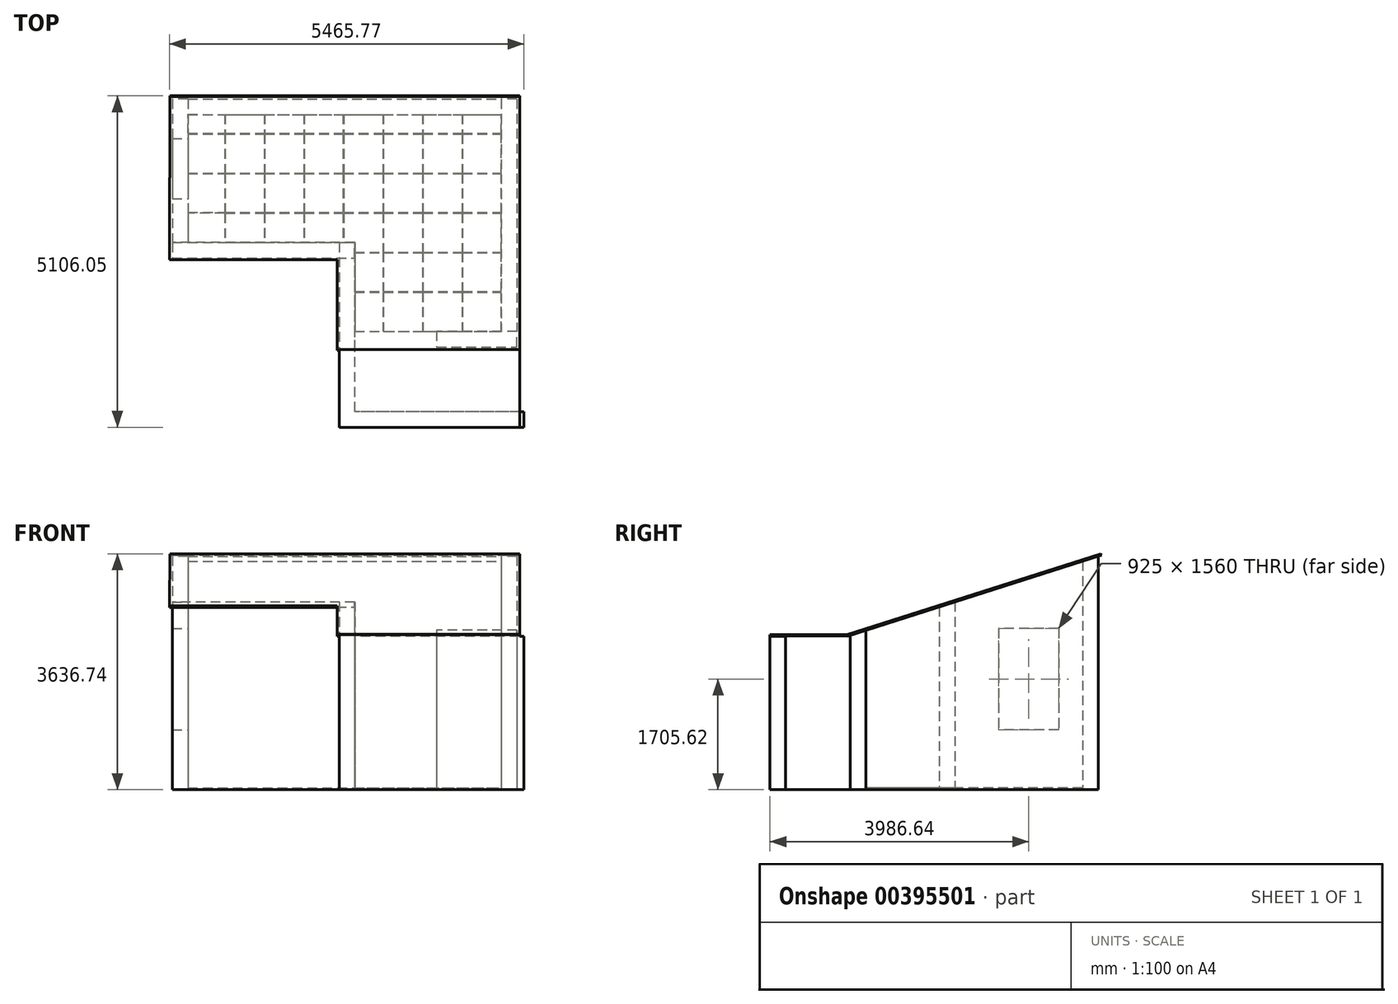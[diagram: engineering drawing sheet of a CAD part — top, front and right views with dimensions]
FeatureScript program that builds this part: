
annotation { "Feature Type Name" : "Feature", "Feature Type Description" : "" }
export const myFeature = defineFeature(function(context is Context, id is Id, definition is map)
    precondition{}
    {
        {
            var Q0;
            Q0=qCreatedBy(makeId("Top.planeOp"),FACE);
            var sketch = newSketch(context, id + "F0", { "sketchPlane" : qUnion([Q0])});
            skLineSegment(sketch, "E0.bottom", {"start": v(-2414.8, 666.08) * mm, "end": v(2415.2, 666.08) * mm});
            skLineSegment(sketch, "E0.top", {"start": v(155.2, -2673.92) * mm, "end": v(2415.2, -2673.92) * mm});
            skLineSegment(sketch, "E0.left", {"start": v(-2414.8, 666.08) * mm, "end": v(-2414.8, -1303.92) * mm});
            skLineSegment(sketch, "E0.right", {"start": v(2415.2, 666.08) * mm, "end": v(2415.2, -2673.92) * mm});
            skLineSegment(sketch, "E1.bottom", {"start": v(-2414.8, -1303.92) * mm, "end": v(155.2, -1303.92) * mm});
            skLineSegment(sketch, "E2", {"start": v(155.2, -1303.92) * mm, "end": v(155.2, -2673.92) * mm});
            skLineSegment(sketch, "E3.top", {"start": v(1817.14, -2673.92) * mm, "end": v(2415.2, -2673.92) * mm});
            skLineSegment(sketch, "E4.top", {"start": v(1208.14, -2673.92) * mm, "end": v(1808.14, -2673.92) * mm});
            skLineSegment(sketch, "E5.top", {"start": v(597, -2673.92) * mm, "end": v(1197, -2673.92) * mm});
            skLineSegment(sketch, "E6.top", {"start": v(155.2, -2673.92) * mm, "end": v(588, -2673.92) * mm});
            skSolve(sketch);
        }
        {
            var Q0;
            Q0=qCreatedBy(makeId("Top.planeOp"),FACE);
            var sketch = newSketch(context, id + "F1", { "sketchPlane" : qUnion([Q0])});
            skLineSegment(sketch, "E7.bottom", {"start": v(1816.8, -2073.43) * mm, "end": v(2414.86, -2073.43) * mm});
            skLineSegment(sketch, "E7.top", {"start": v(1816.8, -2673.43) * mm, "end": v(2414.86, -2673.43) * mm});
            skLineSegment(sketch, "E7.left", {"start": v(1816.8, -2073.43) * mm, "end": v(1816.8, -2673.43) * mm});
            skLineSegment(sketch, "E8.bottom", {"start": v(1816.8, -1461.43) * mm, "end": v(2414.86, -1461.43) * mm});
            skLineSegment(sketch, "E8.top", {"start": v(1816.8, -2061.43) * mm, "end": v(2414.86, -2061.43) * mm});
            skLineSegment(sketch, "E8.left", {"start": v(1816.8, -1461.43) * mm, "end": v(1816.8, -2061.43) * mm});
            skLineSegment(sketch, "E9.bottom", {"start": v(1816.8, -854.43) * mm, "end": v(2414.86, -854.43) * mm});
            skLineSegment(sketch, "E9.top", {"start": v(1816.8, -1454.43) * mm, "end": v(2414.86, -1454.43) * mm});
            skLineSegment(sketch, "E9.left", {"start": v(1816.8, -854.43) * mm, "end": v(1816.8, -1454.43) * mm});
            skLineSegment(sketch, "E10.bottom", {"start": v(1816.8, -242.43) * mm, "end": v(2414.86, -242.43) * mm});
            skLineSegment(sketch, "E10.top", {"start": v(1816.8, -842.43) * mm, "end": v(2414.86, -842.43) * mm});
            skLineSegment(sketch, "E10.left", {"start": v(1816.8, -242.43) * mm, "end": v(1816.8, -842.43) * mm});
            skLineSegment(sketch, "E11.bottom", {"start": v(1816.8, 365.57) * mm, "end": v(2414.86, 365.57) * mm});
            skLineSegment(sketch, "E11.top", {"start": v(1816.8, -234.43) * mm, "end": v(2414.86, -234.43) * mm});
            skLineSegment(sketch, "E11.left", {"start": v(1816.8, 365.57) * mm, "end": v(1816.8, -234.43) * mm});
            skLineSegment(sketch, "E12.top", {"start": v(1816.8, 377.57) * mm, "end": v(2414.86, 377.57) * mm});
            skLineSegment(sketch, "E12.left", {"start": v(1816.8, 666.57) * mm, "end": v(1816.8, 377.57) * mm});
            skLineSegment(sketch, "E13.bottom", {"start": v(1207.8, -2073.43) * mm, "end": v(1807.8, -2073.43) * mm});
            skLineSegment(sketch, "E13.top", {"start": v(1207.8, -2673.43) * mm, "end": v(1807.8, -2673.43) * mm});
            skLineSegment(sketch, "E13.left", {"start": v(1207.8, -2073.43) * mm, "end": v(1207.8, -2673.43) * mm});
            skLineSegment(sketch, "E13.right", {"start": v(1807.8, -2073.43) * mm, "end": v(1807.8, -2673.43) * mm});
            skLineSegment(sketch, "E14.bottom", {"start": v(1207.8, -1461.43) * mm, "end": v(1807.8, -1461.43) * mm});
            skLineSegment(sketch, "E14.top", {"start": v(1207.8, -2061.43) * mm, "end": v(1807.8, -2061.43) * mm});
            skLineSegment(sketch, "E14.left", {"start": v(1207.8, -1461.43) * mm, "end": v(1207.8, -2061.43) * mm});
            skLineSegment(sketch, "E14.right", {"start": v(1807.8, -1461.43) * mm, "end": v(1807.8, -2061.43) * mm});
            skLineSegment(sketch, "E15.bottom", {"start": v(1207.8, -854.43) * mm, "end": v(1807.8, -854.43) * mm});
            skLineSegment(sketch, "E15.top", {"start": v(1207.8, -1454.43) * mm, "end": v(1807.8, -1454.43) * mm});
            skLineSegment(sketch, "E15.left", {"start": v(1207.8, -854.43) * mm, "end": v(1207.8, -1454.43) * mm});
            skLineSegment(sketch, "E15.right", {"start": v(1807.8, -854.43) * mm, "end": v(1807.8, -1454.43) * mm});
            skLineSegment(sketch, "E16.bottom", {"start": v(1207.8, -242.43) * mm, "end": v(1807.8, -242.43) * mm});
            skLineSegment(sketch, "E16.top", {"start": v(1207.8, -842.43) * mm, "end": v(1807.8, -842.43) * mm});
            skLineSegment(sketch, "E16.left", {"start": v(1207.8, -242.43) * mm, "end": v(1207.8, -842.43) * mm});
            skLineSegment(sketch, "E16.right", {"start": v(1807.8, -242.43) * mm, "end": v(1807.8, -842.43) * mm});
            skLineSegment(sketch, "E17.bottom", {"start": v(1207.8, 365.57) * mm, "end": v(1807.8, 365.57) * mm});
            skLineSegment(sketch, "E17.top", {"start": v(1207.8, -234.43) * mm, "end": v(1807.8, -234.43) * mm});
            skLineSegment(sketch, "E17.left", {"start": v(1207.8, 365.57) * mm, "end": v(1207.8, -234.43) * mm});
            skLineSegment(sketch, "E17.right", {"start": v(1807.8, 365.57) * mm, "end": v(1807.8, -234.43) * mm});
            skLineSegment(sketch, "E18.top", {"start": v(1207.8, 377.57) * mm, "end": v(1807.8, 377.57) * mm});
            skLineSegment(sketch, "E18.left", {"start": v(1207.8, 666.57) * mm, "end": v(1207.8, 377.57) * mm});
            skLineSegment(sketch, "E18.right", {"start": v(1807.8, 666.57) * mm, "end": v(1807.8, 377.57) * mm});
            skLineSegment(sketch, "E19.bottom", {"start": v(596.66, -2073.43) * mm, "end": v(1196.66, -2073.43) * mm});
            skLineSegment(sketch, "E19.top", {"start": v(596.66, -2673.43) * mm, "end": v(1196.66, -2673.43) * mm});
            skLineSegment(sketch, "E19.left", {"start": v(596.66, -2073.43) * mm, "end": v(596.66, -2673.43) * mm});
            skLineSegment(sketch, "E19.right", {"start": v(1196.66, -2073.43) * mm, "end": v(1196.66, -2673.43) * mm});
            skLineSegment(sketch, "E20.bottom", {"start": v(596.66, -1461.43) * mm, "end": v(1196.66, -1461.43) * mm});
            skLineSegment(sketch, "E20.top", {"start": v(596.66, -2061.43) * mm, "end": v(1196.66, -2061.43) * mm});
            skLineSegment(sketch, "E20.left", {"start": v(596.66, -1461.43) * mm, "end": v(596.66, -2061.43) * mm});
            skLineSegment(sketch, "E20.right", {"start": v(1196.66, -1461.43) * mm, "end": v(1196.66, -2061.43) * mm});
            skLineSegment(sketch, "E21.bottom", {"start": v(596.66, -854.43) * mm, "end": v(1196.66, -854.43) * mm});
            skLineSegment(sketch, "E21.top", {"start": v(596.66, -1454.43) * mm, "end": v(1196.66, -1454.43) * mm});
            skLineSegment(sketch, "E21.left", {"start": v(596.66, -854.43) * mm, "end": v(596.66, -1454.43) * mm});
            skLineSegment(sketch, "E21.right", {"start": v(1196.66, -854.43) * mm, "end": v(1196.66, -1454.43) * mm});
            skLineSegment(sketch, "E22.bottom", {"start": v(596.66, -242.43) * mm, "end": v(1196.66, -242.43) * mm});
            skLineSegment(sketch, "E22.top", {"start": v(596.66, -842.43) * mm, "end": v(1196.66, -842.43) * mm});
            skLineSegment(sketch, "E22.left", {"start": v(596.66, -242.43) * mm, "end": v(596.66, -842.43) * mm});
            skLineSegment(sketch, "E22.right", {"start": v(1196.66, -242.43) * mm, "end": v(1196.66, -842.43) * mm});
            skLineSegment(sketch, "E23.bottom", {"start": v(596.66, 365.57) * mm, "end": v(1196.66, 365.57) * mm});
            skLineSegment(sketch, "E23.top", {"start": v(596.66, -234.43) * mm, "end": v(1196.66, -234.43) * mm});
            skLineSegment(sketch, "E23.left", {"start": v(596.66, 365.57) * mm, "end": v(596.66, -234.43) * mm});
            skLineSegment(sketch, "E23.right", {"start": v(1196.66, 365.57) * mm, "end": v(1196.66, -234.43) * mm});
            skLineSegment(sketch, "E24.top", {"start": v(596.66, 377.57) * mm, "end": v(1196.66, 377.57) * mm});
            skLineSegment(sketch, "E24.left", {"start": v(596.66, 666.57) * mm, "end": v(596.66, 377.57) * mm});
            skLineSegment(sketch, "E24.right", {"start": v(1196.66, 666.57) * mm, "end": v(1196.66, 377.57) * mm});
            skLineSegment(sketch, "E25.bottom", {"start": v(154.86, -2073.43) * mm, "end": v(587.66, -2073.43) * mm});
            skLineSegment(sketch, "E25.top", {"start": v(154.86, -2673.43) * mm, "end": v(587.66, -2673.43) * mm});
            skLineSegment(sketch, "E25.right", {"start": v(587.66, -2073.43) * mm, "end": v(587.66, -2673.43) * mm});
            skLineSegment(sketch, "E26.bottom", {"start": v(154.86, -1461.43) * mm, "end": v(587.66, -1461.43) * mm});
            skLineSegment(sketch, "E26.top", {"start": v(154.86, -2061.43) * mm, "end": v(587.66, -2061.43) * mm});
            skLineSegment(sketch, "E26.right", {"start": v(587.66, -1461.43) * mm, "end": v(587.66, -2061.43) * mm});
            skLineSegment(sketch, "E27.bottom", {"start": v(-12.34, -854.43) * mm, "end": v(587.66, -854.43) * mm});
            skLineSegment(sketch, "E27.top", {"start": v(154.86, -1454.43) * mm, "end": v(587.66, -1454.43) * mm});
            skLineSegment(sketch, "E27.left", {"start": v(-12.34, -854.43) * mm, "end": v(-12.34, -1303.43) * mm});
            skLineSegment(sketch, "E27.right", {"start": v(587.66, -854.43) * mm, "end": v(587.66, -1454.43) * mm});
            skLineSegment(sketch, "E28.bottom", {"start": v(-12.34, -242.43) * mm, "end": v(587.66, -242.43) * mm});
            skLineSegment(sketch, "E28.top", {"start": v(-12.34, -842.43) * mm, "end": v(587.66, -842.43) * mm});
            skLineSegment(sketch, "E28.left", {"start": v(-12.34, -242.43) * mm, "end": v(-12.34, -842.43) * mm});
            skLineSegment(sketch, "E28.right", {"start": v(587.66, -242.43) * mm, "end": v(587.66, -842.43) * mm});
            skLineSegment(sketch, "E29.bottom", {"start": v(-12.34, 365.57) * mm, "end": v(587.66, 365.57) * mm});
            skLineSegment(sketch, "E29.top", {"start": v(-12.34, -234.43) * mm, "end": v(587.66, -234.43) * mm});
            skLineSegment(sketch, "E29.left", {"start": v(-12.34, 365.57) * mm, "end": v(-12.34, -234.43) * mm});
            skLineSegment(sketch, "E29.right", {"start": v(587.66, 365.57) * mm, "end": v(587.66, -234.43) * mm});
            skLineSegment(sketch, "E30.top", {"start": v(-12.34, 377.57) * mm, "end": v(587.66, 377.57) * mm});
            skLineSegment(sketch, "E30.left", {"start": v(-12.34, 666.57) * mm, "end": v(-12.34, 377.57) * mm});
            skLineSegment(sketch, "E30.right", {"start": v(587.66, 666.57) * mm, "end": v(587.66, 377.57) * mm});
            skLineSegment(sketch, "E31.bottom", {"start": v(-623.48, -853.94) * mm, "end": v(-23.48, -853.94) * mm});
            skLineSegment(sketch, "E31.left", {"start": v(-623.48, -853.94) * mm, "end": v(-623.48, -1303.43) * mm});
            skLineSegment(sketch, "E31.right", {"start": v(-23.48, -853.94) * mm, "end": v(-23.48, -1303.43) * mm});
            skLineSegment(sketch, "E32.bottom", {"start": v(-623.48, -241.94) * mm, "end": v(-23.48, -241.94) * mm});
            skLineSegment(sketch, "E32.top", {"start": v(-623.48, -841.94) * mm, "end": v(-23.48, -841.94) * mm});
            skLineSegment(sketch, "E32.left", {"start": v(-623.48, -241.94) * mm, "end": v(-623.48, -841.94) * mm});
            skLineSegment(sketch, "E32.right", {"start": v(-23.48, -241.94) * mm, "end": v(-23.48, -841.94) * mm});
            skLineSegment(sketch, "E33.bottom", {"start": v(-623.48, 366.06) * mm, "end": v(-23.48, 366.06) * mm});
            skLineSegment(sketch, "E33.top", {"start": v(-623.48, -233.94) * mm, "end": v(-23.48, -233.94) * mm});
            skLineSegment(sketch, "E33.left", {"start": v(-623.48, 366.06) * mm, "end": v(-623.48, -233.94) * mm});
            skLineSegment(sketch, "E33.right", {"start": v(-23.48, 366.06) * mm, "end": v(-23.48, -233.94) * mm});
            skLineSegment(sketch, "E34.top", {"start": v(-623.48, 378.06) * mm, "end": v(-23.48, 378.06) * mm});
            skLineSegment(sketch, "E34.left", {"start": v(-623.48, 666.57) * mm, "end": v(-623.48, 378.06) * mm});
            skLineSegment(sketch, "E34.right", {"start": v(-23.48, 666.57) * mm, "end": v(-23.48, 378.06) * mm});
            skLineSegment(sketch, "E35.bottom", {"start": v(-1232.48, -853.94) * mm, "end": v(-632.48, -853.94) * mm});
            skLineSegment(sketch, "E35.left", {"start": v(-1232.48, -853.94) * mm, "end": v(-1232.48, -1303.43) * mm});
            skLineSegment(sketch, "E35.right", {"start": v(-632.48, -853.94) * mm, "end": v(-632.48, -1303.43) * mm});
            skLineSegment(sketch, "E36.bottom", {"start": v(-1232.48, -241.94) * mm, "end": v(-632.48, -241.94) * mm});
            skLineSegment(sketch, "E36.top", {"start": v(-1232.48, -841.94) * mm, "end": v(-632.48, -841.94) * mm});
            skLineSegment(sketch, "E36.left", {"start": v(-1232.48, -241.94) * mm, "end": v(-1232.48, -841.94) * mm});
            skLineSegment(sketch, "E36.right", {"start": v(-632.48, -241.94) * mm, "end": v(-632.48, -841.94) * mm});
            skLineSegment(sketch, "E37.bottom", {"start": v(-1232.48, 366.06) * mm, "end": v(-632.48, 366.06) * mm});
            skLineSegment(sketch, "E37.top", {"start": v(-1232.48, -233.94) * mm, "end": v(-632.48, -233.94) * mm});
            skLineSegment(sketch, "E37.left", {"start": v(-1232.48, 366.06) * mm, "end": v(-1232.48, -233.94) * mm});
            skLineSegment(sketch, "E37.right", {"start": v(-632.48, 366.06) * mm, "end": v(-632.48, -233.94) * mm});
            skLineSegment(sketch, "E38.top", {"start": v(-1232.48, 378.06) * mm, "end": v(-632.48, 378.06) * mm});
            skLineSegment(sketch, "E38.left", {"start": v(-1232.48, 666.57) * mm, "end": v(-1232.48, 378.06) * mm});
            skLineSegment(sketch, "E38.right", {"start": v(-632.48, 666.57) * mm, "end": v(-632.48, 378.06) * mm});
            skLineSegment(sketch, "E39.bottom", {"start": v(-1841.14, -854.61) * mm, "end": v(-1241.14, -854.61) * mm});
            skLineSegment(sketch, "E39.left", {"start": v(-1841.14, -854.61) * mm, "end": v(-1841.14, -1303.43) * mm});
            skLineSegment(sketch, "E39.right", {"start": v(-1241.14, -854.61) * mm, "end": v(-1241.14, -1303.43) * mm});
            skLineSegment(sketch, "E40.bottom", {"start": v(-1841.14, -242.61) * mm, "end": v(-1241.14, -242.61) * mm});
            skLineSegment(sketch, "E40.top", {"start": v(-1841.14, -842.61) * mm, "end": v(-1241.14, -842.61) * mm});
            skLineSegment(sketch, "E40.left", {"start": v(-1841.14, -242.61) * mm, "end": v(-1841.14, -842.61) * mm});
            skLineSegment(sketch, "E40.right", {"start": v(-1241.14, -242.61) * mm, "end": v(-1241.14, -842.61) * mm});
            skLineSegment(sketch, "E41.bottom", {"start": v(-1841.14, 365.39) * mm, "end": v(-1241.14, 365.39) * mm});
            skLineSegment(sketch, "E41.top", {"start": v(-1841.14, -234.61) * mm, "end": v(-1241.14, -234.61) * mm});
            skLineSegment(sketch, "E41.left", {"start": v(-1841.14, 365.39) * mm, "end": v(-1841.14, -234.61) * mm});
            skLineSegment(sketch, "E41.right", {"start": v(-1241.14, 365.39) * mm, "end": v(-1241.14, -234.61) * mm});
            skLineSegment(sketch, "E42.top", {"start": v(-1841.14, 377.39) * mm, "end": v(-1241.14, 377.39) * mm});
            skLineSegment(sketch, "E42.left", {"start": v(-1841.14, 666.57) * mm, "end": v(-1841.14, 377.39) * mm});
            skLineSegment(sketch, "E42.right", {"start": v(-1241.14, 666.57) * mm, "end": v(-1241.14, 377.39) * mm});
            skLineSegment(sketch, "E43.right", {"start": v(-1850.14, -854.61) * mm, "end": v(-1850.14, -1303.43) * mm});
            skLineSegment(sketch, "E44.bottom", {"start": v(-2415.14, -242.61) * mm, "end": v(-1850.14, -242.61) * mm});
            skLineSegment(sketch, "E44.top", {"start": v(-2415.14, -842.61) * mm, "end": v(-1850.14, -842.61) * mm});
            skLineSegment(sketch, "E44.right", {"start": v(-1850.14, -242.61) * mm, "end": v(-1850.14, -842.61) * mm});
            skLineSegment(sketch, "E45.bottom", {"start": v(-2415.14, 365.39) * mm, "end": v(-1850.14, 365.39) * mm});
            skLineSegment(sketch, "E45.top", {"start": v(-2415.14, -234.61) * mm, "end": v(-1850.14, -234.61) * mm});
            skLineSegment(sketch, "E45.right", {"start": v(-1850.14, 365.39) * mm, "end": v(-1850.14, -234.61) * mm});
            skLineSegment(sketch, "E46.top", {"start": v(-2415.14, 377.39) * mm, "end": v(-1850.14, 377.39) * mm});
            skLineSegment(sketch, "E46.right", {"start": v(-1850.14, 666.57) * mm, "end": v(-1850.14, 377.39) * mm});
            skLineSegment(sketch, "E47", {"start": v(-1841.14, 666.57) * mm, "end": v(-1241.14, 666.57) * mm});
            skLineSegment(sketch, "E48", {"start": v(-1232.48, 666.57) * mm, "end": v(-632.48, 666.57) * mm});
            skLineSegment(sketch, "E49", {"start": v(-623.48, 666.57) * mm, "end": v(-23.48, 666.57) * mm});
            skLineSegment(sketch, "E50.trimOffspring", {"start": v(-12.34, 666.57) * mm, "end": v(587.66, 666.57) * mm});
            skLineSegment(sketch, "E51.trimOffspring", {"start": v(596.66, 666.57) * mm, "end": v(1196.66, 666.57) * mm});
            skLineSegment(sketch, "E52.trimOffspring", {"start": v(1207.8, 666.57) * mm, "end": v(1807.8, 666.57) * mm});
            skLineSegment(sketch, "E53", {"start": v(-1841.14, -1303.43) * mm, "end": v(-1241.14, -1303.43) * mm});
            skLineSegment(sketch, "E54", {"start": v(154.86, -1461.43) * mm, "end": v(154.86, -2061.43) * mm});
            skLineSegment(sketch, "E55", {"start": v(2414.86, -2673.43) * mm, "end": v(2414.86, -2073.43) * mm});
            skLineSegment(sketch, "E56", {"start": v(-2415.14, 365.39) * mm, "end": v(-2415.14, -234.61) * mm});
            skLineSegment(sketch, "E57.trimOffspring", {"start": v(-2415.14, -242.61) * mm, "end": v(-2415.14, -842.61) * mm});
            skLineSegment(sketch, "E58.trimOffspring", {"start": v(-1232.48, -1303.43) * mm, "end": v(-632.48, -1303.43) * mm});
            skLineSegment(sketch, "E59.trimOffspring", {"start": v(-623.48, -1303.43) * mm, "end": v(-23.48, -1303.43) * mm});
            skLineSegment(sketch, "E60.trimOffspring", {"start": v(154.86, -2073.43) * mm, "end": v(154.86, -2673.43) * mm});
            skLineSegment(sketch, "E61.trimOffspring", {"start": v(2414.86, -2061.43) * mm, "end": v(2414.86, -1461.43) * mm});
            skLineSegment(sketch, "E62.trimOffspring", {"start": v(2414.86, -1454.43) * mm, "end": v(2414.86, -854.43) * mm});
            skLineSegment(sketch, "E63.trimOffspring", {"start": v(2414.86, -234.43) * mm, "end": v(2414.86, 365.57) * mm});
            skLineSegment(sketch, "E64.trimOffspring", {"start": v(2414.86, -842.43) * mm, "end": v(2414.86, -242.43) * mm});
            skLineSegment(sketch, "E65", {"start": v(-12.34, -1303.43) * mm, "end": v(150.6, -1303.43) * mm});
            skLineSegment(sketch, "E66", {"start": v(154.86, -1454.43) * mm, "end": v(154.86, -1303.43) * mm});
            skLineSegment(sketch, "E67", {"start": v(154.86, -1303.43) * mm, "end": v(150.6, -1303.43) * mm});
            skLineSegment(sketch, "E68", {"start": v(-2415.14, -854.61) * mm, "end": v(-2415.14, -1303.43) * mm});
            skLineSegment(sketch, "E69", {"start": v(-2415.14, -1303.43) * mm, "end": v(-1850.14, -1303.43) * mm});
            skLineSegment(sketch, "E70", {"start": v(-1850.14, -854.61) * mm, "end": v(-2415.14, -854.61) * mm});
            skLineSegment(sketch, "E71", {"start": v(-2415.14, 377.39) * mm, "end": v(-2415.14, 668.94) * mm});
            skLineSegment(sketch, "E72", {"start": v(-2415.14, 668.94) * mm, "end": v(-1850.14, 666.57) * mm});
            skLineSegment(sketch, "E73", {"start": v(1816.8, 666.57) * mm, "end": v(2411.54, 666.57) * mm});
            skLineSegment(sketch, "E74", {"start": v(2414.86, 377.57) * mm, "end": v(2411.54, 666.57) * mm});
            skSolve(sketch);
        }
        {
            var Q0;
            Q0=makeQuery(id+"F0.imprint","IMPRINT",FACE,{"disambiguationData":[TD([[makeQuery(id+"F0.imprint","IMPRINT",EDGE,{"derivedFrom":sQuery(id+"F0.wireOp",EDGE,"E0.bottom")}),-1.0]])]});
            var sketch = newSketch(context, id + "F2", { "sketchPlane" : qUnion([Q0])});
            skLineSegment(sketch, "E75.bottom", {"start": v(-2414.8, 906.08) * mm, "end": v(2415.2, 906.08) * mm});
            skLineSegment(sketch, "E75.top", {"start": v(-2414.8, 666.08) * mm, "end": v(2415.2, 666.08) * mm});
            skLineSegment(sketch, "E75.left", {"start": v(-2414.8, 906.08) * mm, "end": v(-2414.8, 666.08) * mm});
            skLineSegment(sketch, "E75.right", {"start": v(2415.2, 906.08) * mm, "end": v(2415.2, 666.08) * mm});
            skSolve(sketch);
        }
        {
            var Q0;
            Q0=makeQuery(id+"F0.imprint","IMPRINT",FACE,{"disambiguationData":[TD([[makeQuery(id+"F0.imprint","IMPRINT",EDGE,{"derivedFrom":sQuery(id+"F0.wireOp",EDGE,"E0.bottom")}),-1.0]])]});
            var sketch = newSketch(context, id + "F3", { "sketchPlane" : qUnion([Q0])});
            skLineSegment(sketch, "E76.bottom", {"start": v(2655.2, 906.25) * mm, "end": v(2415.2, 906.25) * mm});
            skLineSegment(sketch, "E76.top", {"start": v(2655.2, -2673.75) * mm, "end": v(2415.2, -2673.75) * mm});
            skLineSegment(sketch, "E76.left", {"start": v(2655.2, 906.25) * mm, "end": v(2655.2, -2673.75) * mm});
            skLineSegment(sketch, "E76.right", {"start": v(2415.2, 906.25) * mm, "end": v(2415.2, -2673.75) * mm});
            skSolve(sketch);
        }
        {
            var Q0;
            Q0=qCreatedBy(makeId("Top.planeOp"),FACE);
            var sketch = newSketch(context, id + "F4", { "sketchPlane" : qUnion([Q0])});
            skLineSegment(sketch, "E77.0", {"start": v(-2416, 906.05) * mm, "end": v(-2415.95, -1303.92) * mm});
            skLineSegment(sketch, "E78", {"start": v(-2416, 906.05) * mm, "end": v(-2655.95, 906.04) * mm});
            skLineSegment(sketch, "E79", {"start": v(-2655.95, 906.04) * mm, "end": v(-2655.95, -1303.92) * mm});
            skLineSegment(sketch, "E80", {"start": v(-2655.95, -1303.92) * mm, "end": v(-2415.95, -1303.92) * mm});
            skSolve(sketch);
        }
        {
            var Q0;
            Q0=qCreatedBy(makeId("Top.planeOp"),FACE);
            var sketch = newSketch(context, id + "F5", { "sketchPlane" : qUnion([Q0])});
            skLineSegment(sketch, "E81.0.2", {"start": v(154.04, -1543.94) * mm, "end": v(154.04, -1303.94) * mm});
            skLineSegment(sketch, "E81.0.3", {"start": v(154.04, -1303.94) * mm, "end": v(-2655.96, -1303.94) * mm});
            skLineSegment(sketch, "E81.0.4", {"start": v(-2655.96, -1303.94) * mm, "end": v(-2655.96, -1543.94) * mm});
            skLineSegment(sketch, "E81.0.5", {"start": v(-2655.96, -1543.94) * mm, "end": v(154.04, -1543.94) * mm});
            skSolve(sketch);
        }
        {
            var Q0;
            Q0=qCreatedBy(makeId("Top.planeOp"),FACE);
            var sketch = newSketch(context, id + "F6", { "sketchPlane" : qUnion([Q0])});
            skLineSegment(sketch, "E82.0.0", {"start": v(-84.93, -1303.9) * mm, "end": v(-84.93, -3911.85) * mm});
            skLineSegment(sketch, "E82.0.2", {"start": v(155.08, -3911.85) * mm, "end": v(155.01, -1303.9) * mm});
            skLineSegment(sketch, "E82.0.3", {"start": v(155.01, -1303.9) * mm, "end": v(-84.93, -1303.9) * mm});
            skLineSegment(sketch, "E83.0.0", {"start": v(-84.93, -4151.8) * mm, "end": v(2762.96, -4151.8) * mm});
            skLineSegment(sketch, "E83.0.1", {"start": v(2762.96, -4151.8) * mm, "end": v(2762.96, -3911.78) * mm});
            skLineSegment(sketch, "E83.0.2", {"start": v(2762.96, -3911.78) * mm, "end": v(155.08, -3911.85) * mm});
            skLineSegment(sketch, "E83.0.3", {"start": v(-84.94, -3911.85) * mm, "end": v(-84.93, -4151.8) * mm});
            skLineSegment(sketch, "E84.trimOffspring", {"start": v(-84.93, -3911.85) * mm, "end": v(-84.94, -3911.85) * mm});
            skSolve(sketch);
        }
        {
            var Q0;
            Q0=qCreatedBy(makeId("Top.planeOp"),FACE);
            var sketch = newSketch(context, id + "F7", { "sketchPlane" : qUnion([Q0])});
            skLineSegment(sketch, "E85.0.2", {"start": v(2655.14, -2913.74) * mm, "end": v(2655.14, -2673.74) * mm});
            skLineSegment(sketch, "E85.0.3", {"start": v(2655.14, -2673.74) * mm, "end": v(1415.14, -2673.74) * mm});
            skLineSegment(sketch, "E85.0.4", {"start": v(1415.14, -2673.74) * mm, "end": v(1415.14, -2913.74) * mm});
            skLineSegment(sketch, "E85.0.5", {"start": v(1415.14, -2913.74) * mm, "end": v(2655.14, -2913.74) * mm});
            skSolve(sketch);
        }
        {
            var Q0;
            {var subQ1=sQuery(id+"F2.wireOp",EDGE,"E75.bottom");Q0=makeQuery(id+"F2.imprint","IMPRINT",FACE,{"disambiguationData":[TD([[makeQuery(id+"F2.imprint","IMPRINT",EDGE,{"derivedFrom":subQ1}),-1.0]])]});}
            var Q1;
            {var subQ1=sQuery(id+"F3.wireOp",EDGE,"E76.bottom");Q1=makeQuery(id+"F3.imprint","IMPRINT",FACE,{"disambiguationData":[TD([[makeQuery(id+"F3.imprint","IMPRINT",EDGE,{"derivedFrom":subQ1}),1.0]])]});}
            var Q2;
            Q2=makeQuery(id+"F4.imprint","IMPRINT",FACE,{"disambiguationData":[TD([[makeQuery(id+"F4.imprint","IMPRINT",EDGE,{"derivedFrom":sQuery(id+"F4.wireOp",EDGE,"E77.0")}),-1.0]])]});
            var Q3;
            Q3=makeQuery(id+"F5.imprint","IMPRINT",FACE,{"disambiguationData":[TD([[makeQuery(id+"F5.imprint","IMPRINT",EDGE,{"derivedFrom":sQuery(id+"F5.wireOp",EDGE,"E81.0.2")}),1.0]])]});
            var Q4;
            Q4=makeQuery(id+"F6.imprint","IMPRINT",FACE,{"disambiguationData":[TD([[makeQuery(id+"F6.imprint","IMPRINT",EDGE,{"derivedFrom":sQuery(id+"F6.wireOp",EDGE,"E82.0.0")}),1.0]])]});
            var Q5;
            Q5=makeQuery(id+"F7.imprint","IMPRINT",FACE,{"disambiguationData":[TD([[makeQuery(id+"F7.imprint","IMPRINT",EDGE,{"derivedFrom":sQuery(id+"F7.wireOp",EDGE,"E85.0.2")}),1.0]])]});
            extrude(context, id + "F8", {"entities" : qUnion([Q0, Q1, Q2, Q3, Q4, Q5]), "depth" : 3600 * mm});
        }
        {
            var Q0;
            Q0=qCreatedBy(makeId("Right.planeOp"),FACE);
            var sketch = newSketch(context, id + "F9", { "sketchPlane" : qUnion([Q0])});
            skLineSegment(sketch, "E86", {"start": v(-2947.88, 2370) * mm, "end": v(987.23, 3623.47) * mm});
            skLineSegment(sketch, "E87", {"start": v(987.23, 3623.47) * mm, "end": v(987.23, 4423.14) * mm});
            skLineSegment(sketch, "E88", {"start": v(987.23, 4423.14) * mm, "end": v(-4372.34, 4418.27) * mm});
            skLineSegment(sketch, "E89", {"start": v(-4372.34, 4418.27) * mm, "end": v(-4392.8, 2362.4) * mm});
            skLineSegment(sketch, "E90", {"start": v(-4392.8, 2362.4) * mm, "end": v(-2947.88, 2370) * mm});
            skPoint(sketch, "E91.bottom.start.orphan", {"position": v(-2947.88, 0) * mm});
            skSolve(sketch);
        }
        {
            var Q0;
            Q0=makeQuery(id+"F9.imprint","IMPRINT",FACE,{"disambiguationData":[TD([[makeQuery(id+"F9.imprint","IMPRINT",EDGE,{"derivedFrom":sQuery(id+"F9.wireOp",EDGE,"E86")}),1.0]])]});
            extrude(context, id + "F10", {"entities" : qUnion([Q0]), "operationType" : NewBodyOperationType.REMOVE, "endBound" : BoundingType.SYMMETRIC, "depth" : 7480 * mm});
        }
        {
            var Q0;
            Q0=qCreatedBy(makeId("Right.planeOp"),FACE);
            var sketch = newSketch(context, id + "F11", { "sketchPlane" : qUnion([Q0])});
            skLineSegment(sketch, "E92.bottom", {"start": v(297.21, 2485.62) * mm, "end": v(-627.79, 2485.62) * mm});
            skLineSegment(sketch, "E92.top", {"start": v(297.21, 925.62) * mm, "end": v(-627.79, 925.62) * mm});
            skLineSegment(sketch, "E92.left", {"start": v(297.21, 2485.62) * mm, "end": v(297.21, 925.62) * mm});
            skLineSegment(sketch, "E92.right", {"start": v(-627.79, 2485.62) * mm, "end": v(-627.79, 925.62) * mm});
            skSolve(sketch);
        }
        {
            var Q0;
            Q0=makeQuery(id+"F11.imprint","IMPRINT",FACE,{"disambiguationData":[TD([[makeQuery(id+"F11.imprint","IMPRINT",EDGE,{"derivedFrom":sQuery(id+"F11.wireOp",EDGE,"E92.bottom")}),1.0]])]});
            extrude(context, id + "F12", {"entities" : qUnion([Q0]), "operationType" : NewBodyOperationType.REMOVE, "oppositeDirection" : true, "depth" : 3560 * mm});
        }
        {
            var Q0;
            Q0=makeQuery(id+"F0.imprint","IMPRINT",FACE,{"disambiguationData":[TD([[makeQuery(id+"F0.imprint","IMPRINT",EDGE,{"derivedFrom":sQuery(id+"F0.wireOp",EDGE,"E0.bottom")}),-1.0]])]});
            extrude(context, id + "F13", {"entities" : qUnion([Q0]), "depth" : 25 * mm});
        }
        {
            var Q0;
            Q0=makeQuery(id+"F10.boolean.opBoolean","COPY",FACE,{"disambiguationData":[TD([makeQuery(id+"F8.opExtrude","SWEPT_FACE",FACE,{"disambiguationData":[OSD([sQuery(id+"F3.wireOp",EDGE,"E76.bottom")])]})])],"derivedFrom":makeQuery(id+"F10.opExtrude","SWEPT_FACE",FACE,{"disambiguationData":[OSD([sQuery(id+"F9.wireOp",EDGE,"E86")])]})});
            cPlane(context, id + "F14", {"entities" : qUnion([Q0]), "cplaneType" : CPlaneType.OFFSET, "offset" : 0 * mm, "width" : 150 * mm, "height" : 150 * mm});
        }
        {
            var Q0;
            Q0=qCreatedBy(id+"F14.planeOp",FACE);
            var sketch = newSketch(context, id + "F15", { "sketchPlane" : qUnion([Q0])});
            skLineSegment(sketch, "E93", {"start": v(-2695.62, 2005.67) * mm, "end": v(2697.42, 2005.67) * mm});
            skLineSegment(sketch, "E94", {"start": v(2697.42, 2005.67) * mm, "end": v(2697.42, -2099.74) * mm});
            skLineSegment(sketch, "E95", {"start": v(2697.42, -2099.74) * mm, "end": v(-114.15, -2099.74) * mm});
            skLineSegment(sketch, "E96", {"start": v(-114.15, -2099.74) * mm, "end": v(-114.15, -635.68) * mm});
            skLineSegment(sketch, "E97", {"start": v(-114.15, -635.68) * mm, "end": v(-2702.8, -635.68) * mm});
            skLineSegment(sketch, "E98", {"start": v(-2702.8, -635.68) * mm, "end": v(-2695.62, 2005.67) * mm});
            skSolve(sketch);
        }
        {
            var Q0;
            Q0=makeQuery(id+"F15.imprint","IMPRINT",FACE,{"disambiguationData":[TD([[makeQuery(id+"F15.imprint","IMPRINT",EDGE,{"derivedFrom":sQuery(id+"F15.wireOp",EDGE,"E93")}),-1.0]])]});
            extrude(context, id + "F16", {"entities" : qUnion([Q0]), "depth" : 25 * mm});
        }
        {
            var Q0;
            Q0 = qSketchRegion(id + "F1", true);
            extrude(context, id + "F17", {"entities" : qUnion([Q0]), "depth" : 10 * mm});
        }
        {
            var Q0;
            Q0=makeQuery(id+"F10.boolean.opBoolean","COPY",FACE,{"derivedFrom":makeQuery(id+"F10.opExtrude","SWEPT_FACE",FACE,{"disambiguationData":[OSD([sQuery(id+"F9.wireOp",EDGE,"E90")])]})});
            var sketch = newSketch(context, id + "F18", { "sketchPlane" : qUnion([Q0])});
            skLineSegment(sketch, "E99.bottom", {"start": v(2696.2, -2935.38) * mm, "end": v(-84.93, -2935.38) * mm});
            skLineSegment(sketch, "E99.top", {"start": v(2696.2, -4139.32) * mm, "end": v(-84.93, -4139.32) * mm});
            skLineSegment(sketch, "E99.left", {"start": v(2696.2, -2935.38) * mm, "end": v(2696.2, -4139.32) * mm});
            skLineSegment(sketch, "E99.right", {"start": v(-84.93, -2935.38) * mm, "end": v(-84.93, -4139.32) * mm});
            skSolve(sketch);
        }
        {
            var Q0;
            Q0 = qSketchRegion(id + "F18", true);
            extrude(context, id + "F19", {"entities" : qUnion([Q0]), "operationType" : NewBodyOperationType.ADD, "depth" : 25 * mm});
        }
    });
